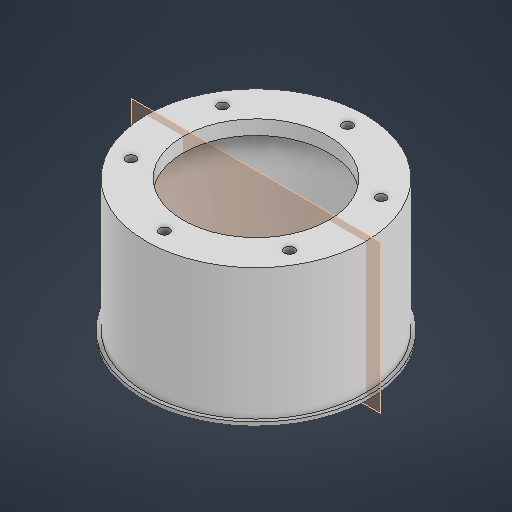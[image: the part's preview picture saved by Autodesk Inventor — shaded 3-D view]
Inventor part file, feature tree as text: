
AUTODESK INVENTOR PART (.ipt)
format: ipt  version: 2025 (Build 290162000, 162)  size: 287,232 bytes
history: native  units: in
note: dims shown in document units (in); Inventor stores cm internally (conversion verified against a paired STEP export)
features: other x12, sketch x6, extrude x5, plane x1
ambient origin geometry x8: Origin, YZ Plane, XZ Plane, XY Plane, X Axis, Y Axis, Z Axis, Center Point
bodies: Solid1 (feature_tree)
feature tree (24):
  other  "Table"
  other  "C .Replace - 01"
  other  "C .Replace - 02"
  other  "C .Replace - 03"
  other  "C .Replace - 04"
  other  "C .Replace - 05"
  other  "C .Replace - 06"
  other  "C .Replace - 07"
  other  "C .Replace - 08"
  other  "C .Replace - 09"
  other  "C .Replace - 10"
  other  "C .Replace - Face"
  sketch  "Sketch1"  dims[d5=0.0in d7=0.0in]
  extrude  "Extrusion1"  TaperAngle=0.0deg  [1 undecoded]
  extrude  "Extrusion2"  Depth=10.0394in
  sketch  "Sketch2"  dims[d28=0.1969in d29=3.937in d31=360.0deg]
  extrude  "Extrusion7"  Depth=3.937in TaperAngle=360.0deg
  plane  "Work Plane2"
  extrude  "Extrusion8"  Depth=0.3937in
  extrude  "Extrusion30"  Depth=0.2165in
  sketch  "Sketch3"  dims[d33=0.3937in d34=0.0in d52=4.5276in]
  sketch  "Sketch Circular Pattern1"  dims[d18=0.0in d27=10.0394in]
  sketch  "Sketch24"  dims[d232=2.3622in d234=360.0deg d236=0.3937in d237=0.0in d113=0.0197in d114=0.0344in d115=0.0197in d116=0.0344in d167=0.0197in d168=0.0344in d169=0.0197in d170=0.0344in d215=0.0197in d216=0.0344in d217=0.0197in d218=0.0344in d219=0.0in d220=0.0in]
  sketch  "Sketch Circular Pattern4"  dims[d230=4.0157in d231=0.2165in]
note: 1 required parameter value undecoded (feature->parameter linkage not recoverable at this tier; creation-order binding heuristic only, values carry confidence <= 0.55)
